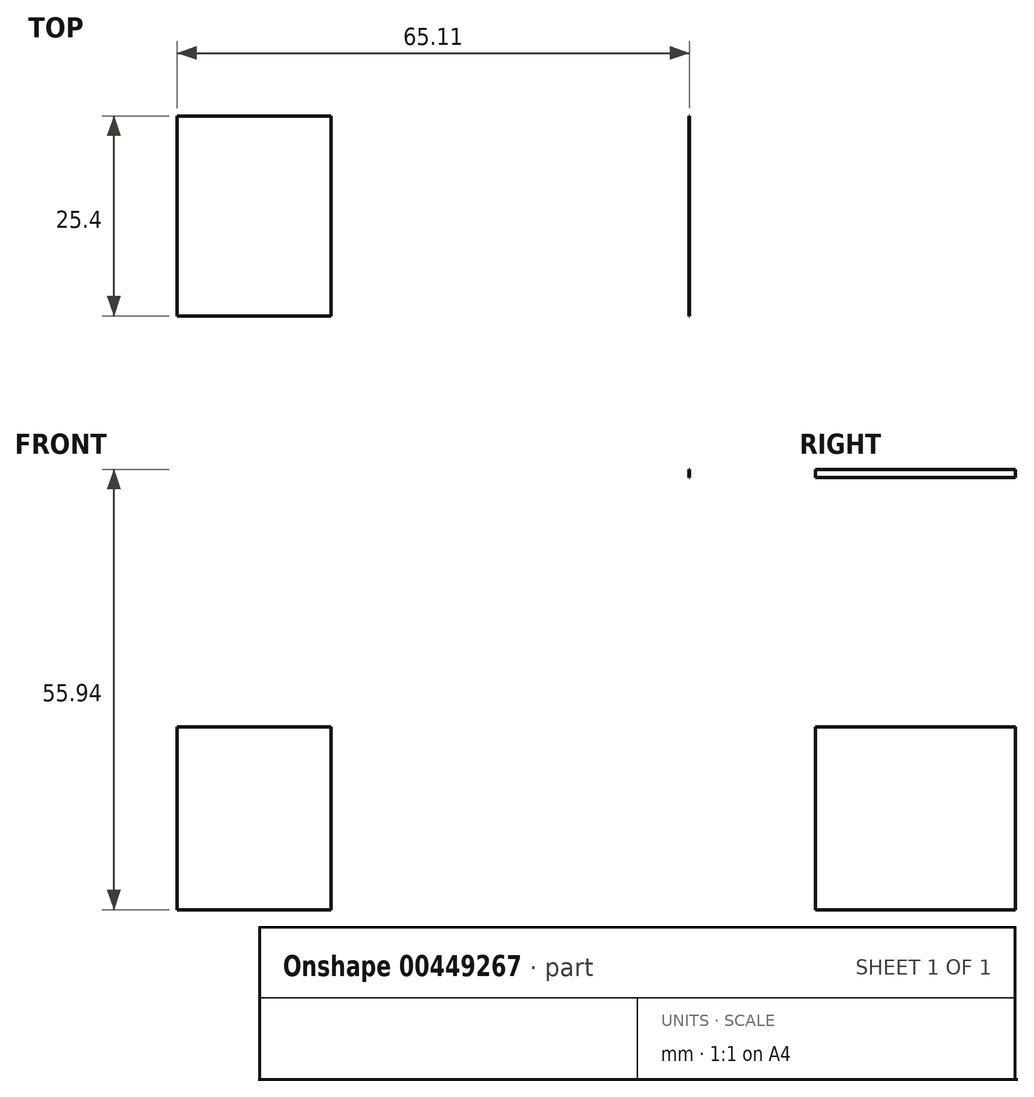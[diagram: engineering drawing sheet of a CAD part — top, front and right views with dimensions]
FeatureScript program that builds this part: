
annotation { "Feature Type Name" : "Feature", "Feature Type Description" : "" }
export const myFeature = defineFeature(function(context is Context, id is Id, definition is map)
    precondition{}
    {
        {
            var Q0;
            Q0=qCreatedBy(makeId("Front.planeOp"),FACE);
            var sketch = newSketch(context, id + "F0", { "sketchPlane" : qUnion([Q0])});
            skLineSegment(sketch, "E0.bottom", {"start": v(74.97, 74.61) * mm, "end": v(75.05, 74.61) * mm});
            skLineSegment(sketch, "E0.top", {"start": v(74.97, 75.67) * mm, "end": v(75.05, 75.67) * mm});
            skLineSegment(sketch, "E0.left", {"start": v(74.97, 74.61) * mm, "end": v(74.97, 75.67) * mm});
            skLineSegment(sketch, "E0.right", {"start": v(75.05, 74.61) * mm, "end": v(75.05, 75.67) * mm});
            skLineSegment(sketch, "E1.bottom", {"start": v(29.53, 42.97) * mm, "end": v(9.94, 42.97) * mm});
            skLineSegment(sketch, "E1.top", {"start": v(29.53, 19.73) * mm, "end": v(9.94, 19.73) * mm});
            skLineSegment(sketch, "E1.left", {"start": v(29.53, 42.97) * mm, "end": v(29.53, 19.73) * mm});
            skLineSegment(sketch, "E1.right", {"start": v(9.94, 42.97) * mm, "end": v(9.94, 19.73) * mm});
            skSolve(sketch);
        }
        {
            var Q0;
            Q0=qCreatedBy(makeId("Front.planeOp"),FACE);
            var sketch = newSketch(context, id + "F1", { "sketchPlane" : qUnion([Q0])});
            skSolve(sketch);
        }
        {
            var Q0;
            Q0 = qSketchRegion(id + "F1", true);
            var Q1;
            Q1 = qSketchRegion(id + "F0", true);
            extrude(context, id + "F2", {"entities" : qUnion([Q0, Q1]), "depth" : 25.4 * mm});
        }
    });
